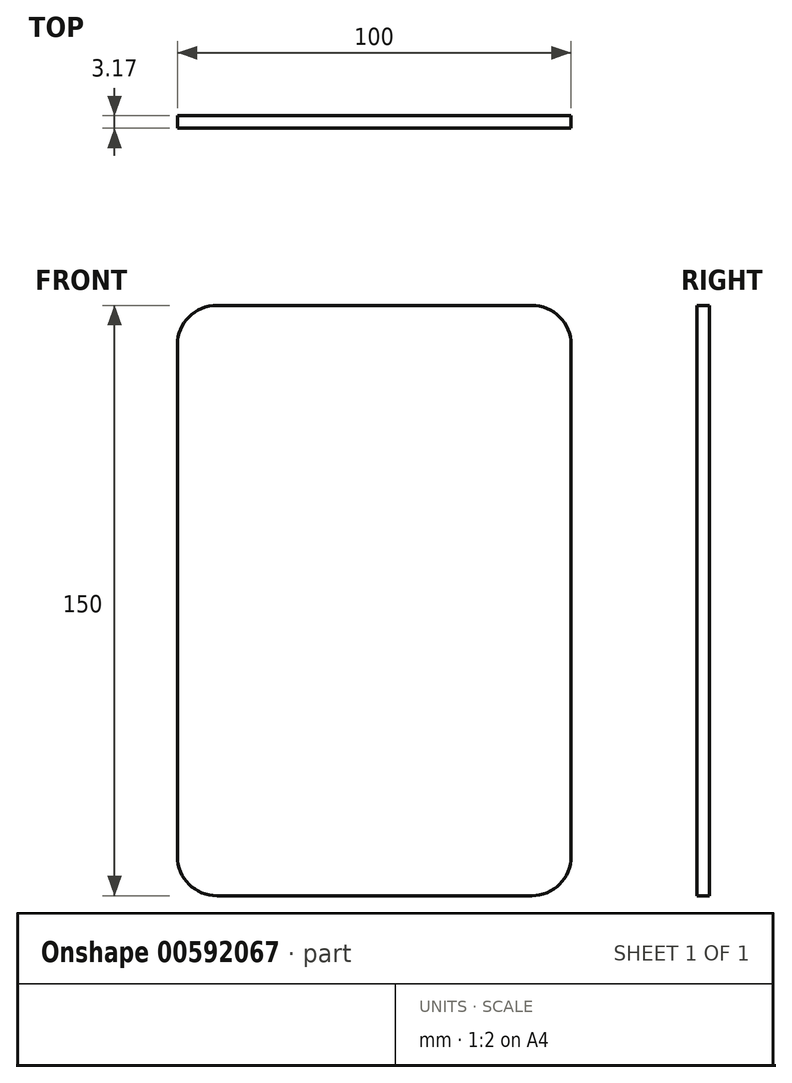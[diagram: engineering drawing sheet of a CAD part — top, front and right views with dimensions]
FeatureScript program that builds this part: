
annotation { "Feature Type Name" : "Feature", "Feature Type Description" : "" }
export const myFeature = defineFeature(function(context is Context, id is Id, definition is map)
    precondition{}
    {
        {
            var Q0;
            Q0=qCreatedBy(makeId("Front.planeOp"),FACE);
            var sketch = newSketch(context, id + "F0", { "sketchPlane" : qUnion([Q0])});
            skLineSegment(sketch, "E0.bottom", {"start": v(-40, 75) * mm, "end": v(40, 75) * mm});
            skLineSegment(sketch, "E0.top", {"start": v(-40, -75) * mm, "end": v(40, -75) * mm});
            skLineSegment(sketch, "E0.left", {"start": v(-50, 65) * mm, "end": v(-50, -65) * mm});
            skLineSegment(sketch, "E0.right", {"start": v(50, 65) * mm, "end": v(50, -65) * mm});
            skLineSegment(sketch, "E1", {"start": v(0, 75) * mm, "end": v(0, -75) * mm, "construction": true});
            skLineSegment(sketch, "E2", {"start": v(-50, 0) * mm, "end": v(50, 0) * mm, "construction": true});
            skPoint(sketch, "E3.visualSharp", {"position": v(-50, 75) * mm});
            skArc(sketch, "E3.filletArc", {"start": v(-40, 75) * mm, "mid": v(-47.07, 72.07) * mm, "end": v(-50, 65) * mm});
            skPoint(sketch, "E4.visualSharp", {"position": v(50, 75) * mm});
            skArc(sketch, "E4.filletArc", {"start": v(50, 65) * mm, "mid": v(47.07, 72.07) * mm, "end": v(40, 75) * mm});
            skPoint(sketch, "E5.visualSharp", {"position": v(50, -75) * mm});
            skArc(sketch, "E5.filletArc", {"start": v(40, -75) * mm, "mid": v(47.07, -72.07) * mm, "end": v(50, -65) * mm});
            skPoint(sketch, "E6.visualSharp", {"position": v(-50, -75) * mm});
            skArc(sketch, "E6.filletArc", {"start": v(-50, -65) * mm, "mid": v(-47.07, -72.07) * mm, "end": v(-40, -75) * mm});
            skLineSegment(sketch, "E7.bottom", {"start": v(-25, 25) * mm, "end": v(25, 25) * mm});
            skLineSegment(sketch, "E7.top", {"start": v(-25, -25) * mm, "end": v(25, -25) * mm});
            skLineSegment(sketch, "E7.left", {"start": v(-25, 25) * mm, "end": v(-25, -25) * mm});
            skLineSegment(sketch, "E7.right", {"start": v(25, 25) * mm, "end": v(25, -25) * mm});
            skLineSegment(sketch, "E8", {"start": v(-25, 25) * mm, "end": v(25, -25) * mm, "construction": true});
            skLineSegment(sketch, "E9", {"start": v(25, 25) * mm, "end": v(-25, -25) * mm, "construction": true});
            skSolve(sketch);
        }
        {
            var Q0;
            Q0 = qSketchRegion(id + "F0", true);
            var Q1;
            Q1=makeQuery(id+"F0.imprint","IMPRINT",FACE,{"disambiguationData":[TD([[makeQuery(id+"F0.imprint","IMPRINT",EDGE,{"derivedFrom":sQuery(id+"F0.wireOp",EDGE,"E7.bottom")}),-1.0]])]});
            extrude(context, id + "F1", {"entities" : qUnion([Q0, Q1]), "depth" : 3.17 * mm, "offsetDistance" : 25 * mm});
        }
    });
